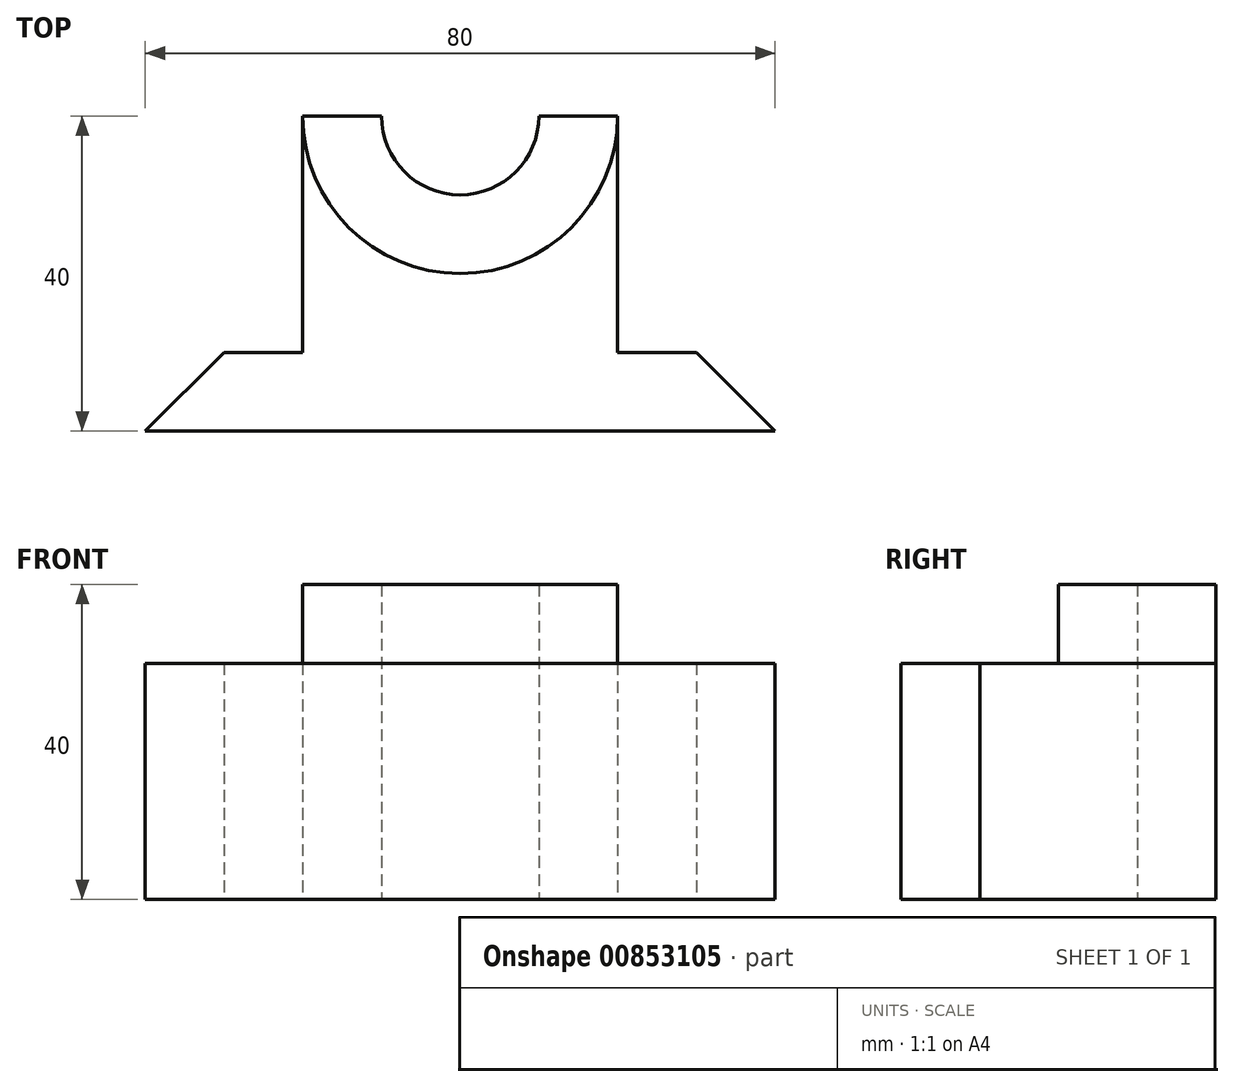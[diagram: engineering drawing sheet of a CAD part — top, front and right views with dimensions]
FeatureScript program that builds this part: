
annotation { "Feature Type Name" : "Feature", "Feature Type Description" : "" }
export const myFeature = defineFeature(function(context is Context, id is Id, definition is map)
    precondition{}
    {
        {
            var Q0;
            Q0=qCreatedBy(makeId("Top.planeOp"),FACE);
            var sketch = newSketch(context, id + "F0", { "sketchPlane" : qUnion([Q0])});
            skLineSegment(sketch, "E0", {"start": v(-40, -20) * mm, "end": v(40, -20) * mm});
            skLineSegment(sketch, "E1", {"start": v(40, -20) * mm, "end": v(30, -10) * mm});
            skLineSegment(sketch, "E2", {"start": v(20, 20) * mm, "end": v(10, 20) * mm});
            skLineSegment(sketch, "E3", {"start": v(-30, -10) * mm, "end": v(-40, -20) * mm});
            skArc(sketch, "E4", {"start": v(-10, 20) * mm, "mid": v(0, 10) * mm, "end": v(10, 20) * mm});
            skLineSegment(sketch, "E5.trimOffspring", {"start": v(-10, 20) * mm, "end": v(-20, 20) * mm});
            skLineSegment(sketch, "E6", {"start": v(-30, -10) * mm, "end": v(-20, -10) * mm});
            skLineSegment(sketch, "E7", {"start": v(-20, 20) * mm, "end": v(-20, -10) * mm});
            skLineSegment(sketch, "E8", {"start": v(20, 20) * mm, "end": v(20, -10) * mm});
            skLineSegment(sketch, "E9.trimOffspring", {"start": v(20, -10) * mm, "end": v(30, -10) * mm});
            skArc(sketch, "E10", {"start": v(-20, 20) * mm, "mid": v(0, 0) * mm, "end": v(20, 20) * mm});
            skSolve(sketch);
        }
        {
            var Q0;
            Q0=makeQuery(id+"F0.imprint","IMPRINT",FACE,{"disambiguationData":[TD([[makeQuery(id+"F0.imprint","IMPRINT",EDGE,{"derivedFrom":sQuery(id+"F0.wireOp",EDGE,"E0")}),1.0]])]});
            extrude(context, id + "F1", {"entities" : qUnion([Q0]), "depth" : 30 * mm, "offsetDistance" : 25 * mm});
        }
        {
            var Q0;
            Q0=makeQuery(id+"F0.imprint","IMPRINT",FACE,{"disambiguationData":[TD([[makeQuery(id+"F0.imprint","IMPRINT",EDGE,{"derivedFrom":sQuery(id+"F0.wireOp",EDGE,"E2")}),1.0]])]});
            extrude(context, id + "F2", {"entities" : qUnion([Q0]), "operationType" : NewBodyOperationType.ADD, "depth" : 40 * mm, "offsetDistance" : 25 * mm});
        }
    });
